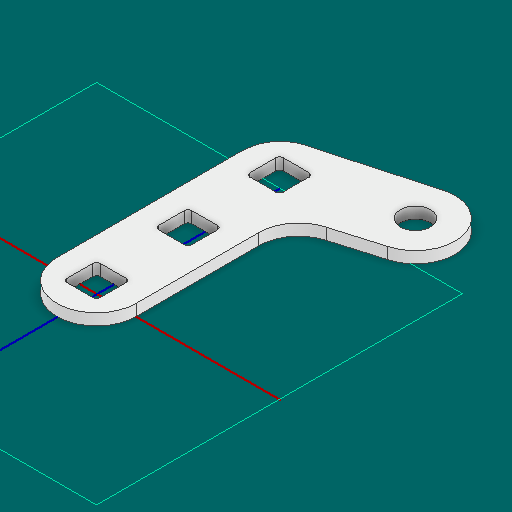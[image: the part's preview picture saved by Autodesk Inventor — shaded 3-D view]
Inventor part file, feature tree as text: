
AUTODESK INVENTOR PART (.ipt)
format: ipt  version: 2025 (Build 290162000, 162)  size: 146,944 bytes
history: native  units: in
note: dims shown in document units (in); Inventor stores cm internally (conversion verified against a paired STEP export)
features: other x3, extrude x1, sketch x1
ambient origin geometry x8: Origin, YZ Plane, XZ Plane, XY Plane, X Axis, Y Axis, Z Axis, Center Point
bodies: Solid1 (feature_tree)
feature tree (5):
  other  "Blocks"
  extrude  "Extrusion1"  Depth=0.2165in
  sketch  "Sketch1"  dims[d0=0.0625in d1=0.0in d8=0.2165in d3=0.5in d4=0.0344in d5=0.5in d6=0.0344in]
  other  "main"
  other  "main:1"
